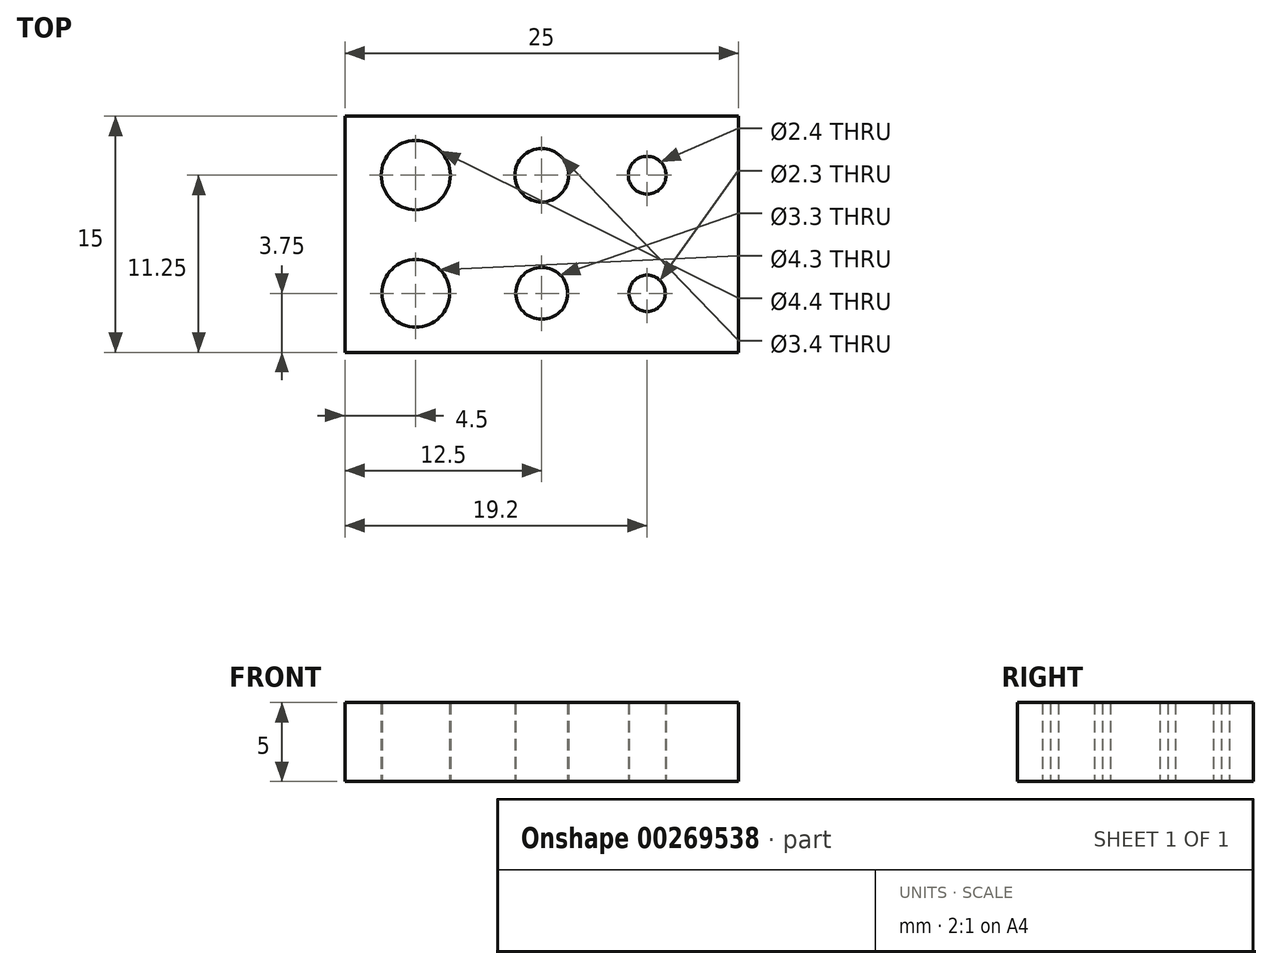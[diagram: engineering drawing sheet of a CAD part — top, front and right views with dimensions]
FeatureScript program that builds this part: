
annotation { "Feature Type Name" : "Feature", "Feature Type Description" : "" }
export const myFeature = defineFeature(function(context is Context, id is Id, definition is map)
    precondition{}
    {
        {
            var Q0;
            Q0=qCreatedBy(makeId("Top.planeOp"),FACE);
            var sketch = newSketch(context, id + "F0", { "sketchPlane" : qUnion([Q0])});
            skLineSegment(sketch, "E0.bottom", {"start": v(12.5, 7.5) * mm, "end": v(-12.5, 7.5) * mm});
            skLineSegment(sketch, "E0.top", {"start": v(12.5, -7.5) * mm, "end": v(-12.5, -7.5) * mm});
            skPoint(sketch, "E0.middle", {"position": v(0, 0) * mm});
            skCircle(sketch, "E1", {"center": v(-8, -3.75) * mm, "radius": 2.15 * mm});
            skCircle(sketch, "E2", {"center": v(-8, 3.75) * mm, "radius": 2.2 * mm});
            skCircle(sketch, "E3", {"center": v(0, -3.75) * mm, "radius": 1.65 * mm});
            skCircle(sketch, "E4", {"center": v(0, 3.75) * mm, "radius": 1.7 * mm});
            skCircle(sketch, "E5", {"center": v(6.7, -3.75) * mm, "radius": 1.15 * mm});
            skCircle(sketch, "E6", {"center": v(6.7, 3.75) * mm, "radius": 1.2 * mm});
            skPoint(sketch, "E7", {"position": v(-12.5, 0) * mm});
            skPoint(sketch, "E8", {"position": v(12.5, 0) * mm});
            skPoint(sketch, "E9", {"position": v(-12.5, -3.75) * mm});
            skPoint(sketch, "E10", {"position": v(-12.5, 3.75) * mm});
            skPoint(sketch, "E11", {"position": v(12.5, 3.75) * mm});
            skPoint(sketch, "E12", {"position": v(12.5, -3.75) * mm});
            skLineSegment(sketch, "E13", {"start": v(-12.5, 7.5) * mm, "end": v(-12.5, 0) * mm});
            skLineSegment(sketch, "E14", {"start": v(-12.5, 0) * mm, "end": v(-12.5, -7.5) * mm});
            skLineSegment(sketch, "E15", {"start": v(12.5, -7.5) * mm, "end": v(12.5, 0) * mm});
            skLineSegment(sketch, "E16", {"start": v(12.5, 0) * mm, "end": v(12.5, 7.5) * mm});
            skLineSegment(sketch, "E17", {"start": v(-12.5, -3.75) * mm, "end": v(12.5, -3.75) * mm});
            skLineSegment(sketch, "E18", {"start": v(-12.5, 3.75) * mm, "end": v(12.5, 3.75) * mm});
            skLineSegment(sketch, "E19", {"start": v(-8, 3.75) * mm, "end": v(-8, -3.75) * mm});
            skLineSegment(sketch, "E20", {"start": v(6.7, 3.75) * mm, "end": v(6.7, -3.75) * mm});
            skSolve(sketch);
        }
        {
            var Q0;
            {var subQ9=sQuery(id+"F0.wireOp",EDGE,"E19");var subQ11=sQuery(id+"F0.wireOp",EDGE,"E1");var subQ12=makeQuery(id+"F0.imprint","INTERSECT",VERTEX,{"derivedFrom":[subQ11,subQ9]});Q0=makeQuery(id+"F0.imprint","IMPRINT",FACE,{"disambiguationData":[TD([[makeQuery(id+"F0.imprint","IMPRINT",EDGE,{"disambiguationData":[TD([[subQ12,-1.0]])],"derivedFrom":subQ11}),-1.0]])]});}
            var Q1;
            {var subQ16=sQuery(id+"F0.wireOp",EDGE,"E19");var subQ17=sQuery(id+"F0.wireOp",EDGE,"E1");var subQ18=makeQuery(id+"F0.imprint","INTERSECT",VERTEX,{"derivedFrom":[subQ17,subQ16]});Q1=makeQuery(id+"F0.imprint","IMPRINT",FACE,{"disambiguationData":[TD([[makeQuery(id+"F0.imprint","IMPRINT",EDGE,{"disambiguationData":[TD([[subQ18,1.0]])],"derivedFrom":subQ17}),-1.0]])]});}
            var Q2;
            {var subQ7=sQuery(id+"F0.wireOp",EDGE,"E20");var subQ8=sQuery(id+"F0.wireOp",EDGE,"E5");var subQ9=makeQuery(id+"F0.imprint","INTERSECT",VERTEX,{"derivedFrom":[subQ8,subQ7]});Q2=makeQuery(id+"F0.imprint","IMPRINT",FACE,{"disambiguationData":[TD([[makeQuery(id+"F0.imprint","IMPRINT",EDGE,{"disambiguationData":[TD([[subQ9,1.0]])],"derivedFrom":subQ8}),-1.0]])]});}
            var Q3;
            {var subQ12=sQuery(id+"F0.wireOp",EDGE,"E0.top");Q3=makeQuery(id+"F0.imprint","IMPRINT",FACE,{"disambiguationData":[TD([[makeQuery(id+"F0.imprint","IMPRINT",EDGE,{"derivedFrom":subQ12}),-1.0]])]});}
            var Q4;
            {var subQ12=sQuery(id+"F0.wireOp",EDGE,"E0.bottom");Q4=makeQuery(id+"F0.imprint","IMPRINT",FACE,{"disambiguationData":[TD([[makeQuery(id+"F0.imprint","IMPRINT",EDGE,{"derivedFrom":subQ12}),1.0]])]});}
            extrude(context, id + "F1", {"entities" : qUnion([Q0, Q1, Q2, Q3, Q4]), "depth" : 5 * mm, "offsetDistance" : 25 * mm});
        }
    });
